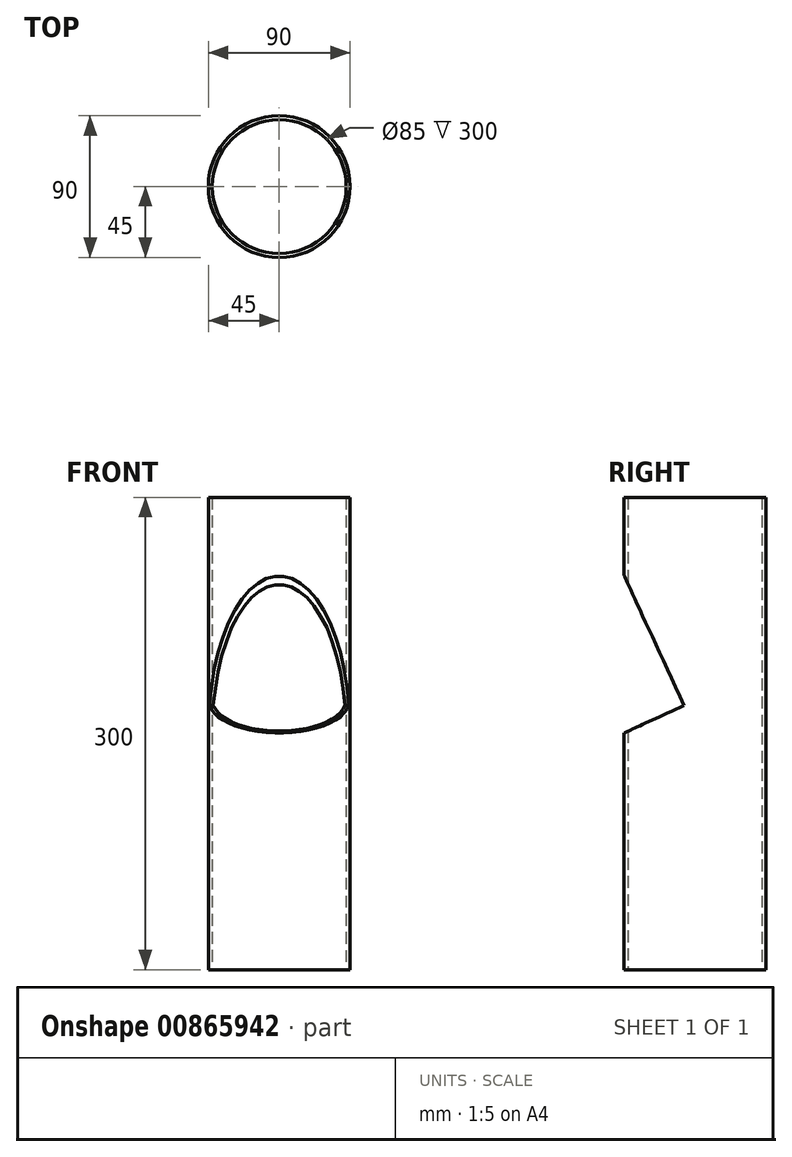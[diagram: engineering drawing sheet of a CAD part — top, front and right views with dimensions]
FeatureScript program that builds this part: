
annotation { "Feature Type Name" : "Feature", "Feature Type Description" : "" }
export const myFeature = defineFeature(function(context is Context, id is Id, definition is map)
    precondition{}
    {
        {
            var Q0;
            Q0=qCreatedBy(makeId("Top.planeOp"),FACE);
            var sketch = newSketch(context, id + "F0", { "sketchPlane" : qUnion([Q0])});
            skCircle(sketch, "E0", {"center": v(0, 0) * mm, "radius": 45 * mm});
            skSolve(sketch);
        }
        {
            var Q0;
            Q0 = qSketchRegion(id + "F0", true);
            extrude(context, id + "F1", {"entities" : qUnion([Q0]), "endBound" : BoundingType.SYMMETRIC, "depth" : 300 * mm, "offsetDistance" : 25 * mm});
        }
        {
            var Q0;
            Q0=makeQuery(id+"F1.opExtrude","CAP_FACE",FACE,{"disambiguationData":[OSD([sQuery(id+"F0.wireOp",EDGE,"E0")])],"isStart":false});
            var Q1;
            Q1=makeQuery(id+"F1.opExtrude","CAP_FACE",FACE,{"disambiguationData":[OSD([sQuery(id+"F0.wireOp",EDGE,"E0")])],"isStart":true});
            shell(context, id + "F2", {"entities" : qUnion([Q0, Q1]), "thickness" : 2.5 * mm});
        }
        {
            var Q0;
            Q0=qCreatedBy(makeId("Right.planeOp"),FACE);
            var sketch = newSketch(context, id + "F3", { "sketchPlane" : qUnion([Q0])});
            skLineSegment(sketch, "E1", {"start": v(-45, 0.39) * mm, "end": v(-45, 100.39) * mm});
            skLineSegment(sketch, "E2", {"start": v(-45, 100.39) * mm, "end": v(-7, 17.9) * mm});
            skLineSegment(sketch, "E3", {"start": v(-7, 17.9) * mm, "end": v(-45, 0.39) * mm});
            skSolve(sketch);
        }
        {
            var Q0;
            Q0 = qSketchRegion(id + "F3", true);
            extrude(context, id + "F4", {"entities" : qUnion([Q0]), "operationType" : NewBodyOperationType.REMOVE, "endBound" : BoundingType.SYMMETRIC, "depth" : 100 * mm, "offsetDistance" : 25 * mm});
        }
    });
